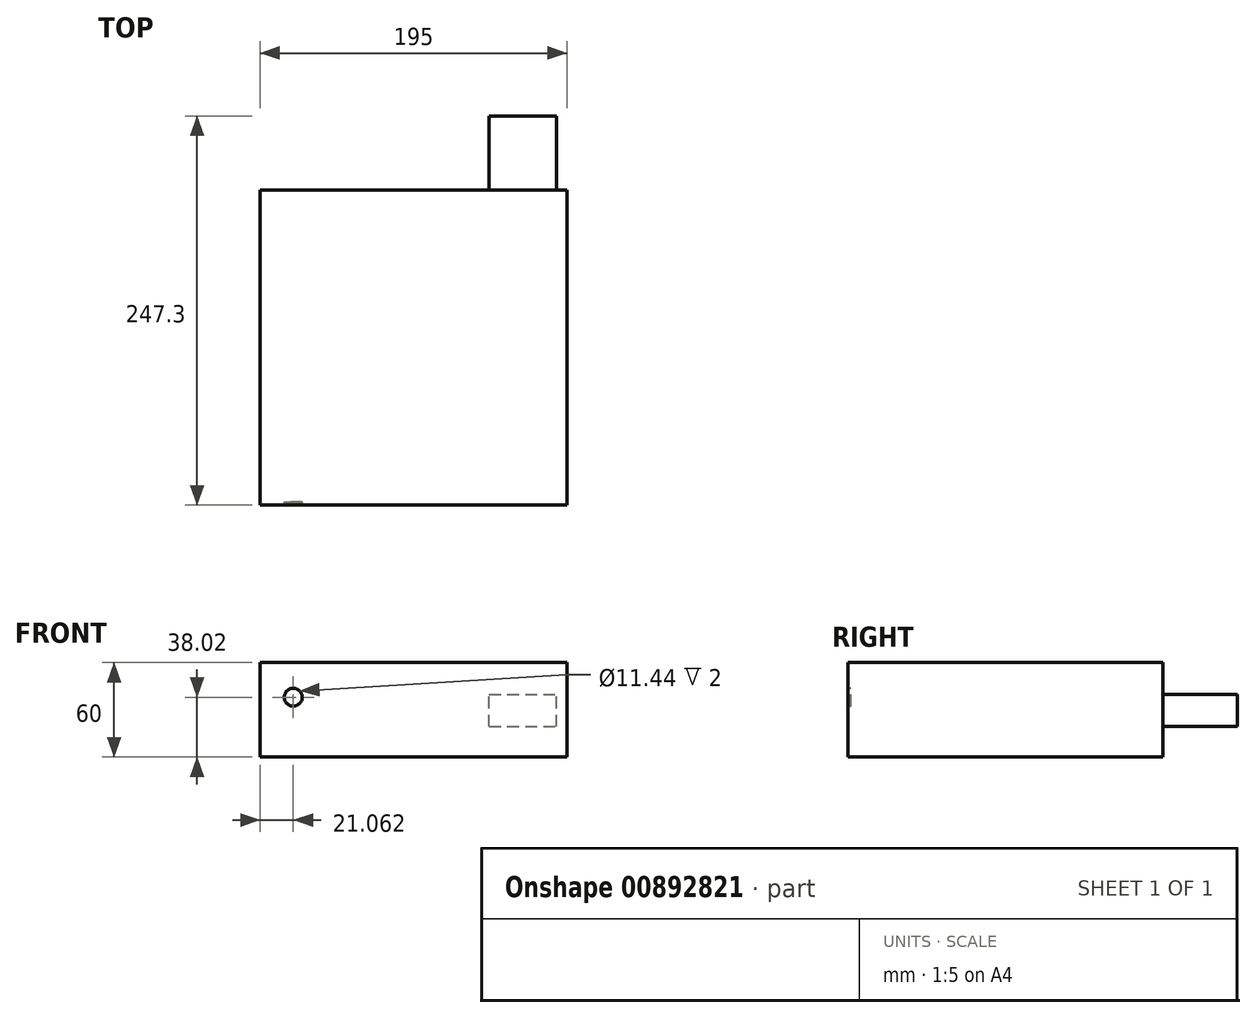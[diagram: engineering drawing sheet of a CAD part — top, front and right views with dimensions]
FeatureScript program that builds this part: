
annotation { "Feature Type Name" : "Feature", "Feature Type Description" : "" }
export const myFeature = defineFeature(function(context is Context, id is Id, definition is map)
    precondition{}
    {
        {
            var Q0;
            Q0=qCreatedBy(makeId("Top.planeOp"),FACE);
            var sketch = newSketch(context, id + "F0", { "sketchPlane" : qUnion([Q0])});
            skLineSegment(sketch, "E0.bottom", {"start": v(-97.5, -100) * mm, "end": v(97.5, -100) * mm});
            skLineSegment(sketch, "E0.top", {"start": v(-97.5, 100) * mm, "end": v(97.5, 100) * mm});
            skLineSegment(sketch, "E0.left", {"start": v(-97.5, -100) * mm, "end": v(-97.5, 100) * mm});
            skLineSegment(sketch, "E0.right", {"start": v(97.5, -100) * mm, "end": v(97.5, 100) * mm});
            skPoint(sketch, "E0.middle", {"position": v(0, 0) * mm});
            skSolve(sketch);
        }
        {
            var Q0;
            Q0=makeQuery(id+"F0.imprint","IMPRINT",FACE,{"disambiguationData":[TD([[makeQuery(id+"F0.imprint","IMPRINT",EDGE,{"derivedFrom":sQuery(id+"F0.wireOp",EDGE,"E0.bottom")}),1.0]])]});
            extrude(context, id + "F1", {"entities" : qUnion([Q0]), "depth" : 60 * mm, "offsetDistance" : 25 * mm});
        }
        {
            var Q0;
            Q0=makeQuery(id+"F1.opExtrude","SWEPT_FACE",FACE,{"disambiguationData":[OSD([sQuery(id+"F0.wireOp",EDGE,"E0.top")])]});
            var sketch = newSketch(context, id + "F2", { "sketchPlane" : qUnion([Q0])});
            skLineSegment(sketch, "E1.bottom", {"start": v(-47.92, 19.43) * mm, "end": v(-90.77, 19.43) * mm});
            skLineSegment(sketch, "E1.top", {"start": v(-47.92, 39.75) * mm, "end": v(-90.77, 39.75) * mm});
            skLineSegment(sketch, "E1.left", {"start": v(-47.92, 19.43) * mm, "end": v(-47.92, 39.75) * mm});
            skLineSegment(sketch, "E1.right", {"start": v(-90.77, 19.43) * mm, "end": v(-90.77, 39.75) * mm});
            skPoint(sketch, "E1.middle", {"position": v(-69.35, 29.59) * mm});
            skSolve(sketch);
        }
        {
            var Q0;
            Q0=makeQuery(id+"F2.imprint","IMPRINT",FACE,{"disambiguationData":[TD([[makeQuery(id+"F2.imprint","IMPRINT",EDGE,{"derivedFrom":sQuery(id+"F2.wireOp",EDGE,"E1.bottom")}),-1.0]])]});
            extrude(context, id + "F3", {"entities" : qUnion([Q0]), "operationType" : NewBodyOperationType.ADD, "depth" : 47.3 * mm, "offsetDistance" : 25 * mm});
        }
        {
            var Q0;
            Q0=makeQuery(id+"F1.opExtrude","SWEPT_FACE",FACE,{"disambiguationData":[OSD([sQuery(id+"F0.wireOp",EDGE,"E0.bottom")])]});
            var sketch = newSketch(context, id + "F4", { "sketchPlane" : qUnion([Q0])});
            skCircle(sketch, "E2", {"center": v(-76.44, 38.02) * mm, "radius": 5.72 * mm});
            skSolve(sketch);
        }
        {
            var Q0;
            Q0=makeQuery(id+"F4.imprint","IMPRINT",FACE,{"disambiguationData":[TD([[makeQuery(id+"F4.imprint","IMPRINT",EDGE,{"derivedFrom":sQuery(id+"F4.wireOp",EDGE,"E2")}),1.0]])]});
            extrude(context, id + "F5", {"entities" : qUnion([Q0]), "operationType" : NewBodyOperationType.REMOVE, "oppositeDirection" : true, "depth" : 2 * mm, "offsetDistance" : 25 * mm});
        }
    });
